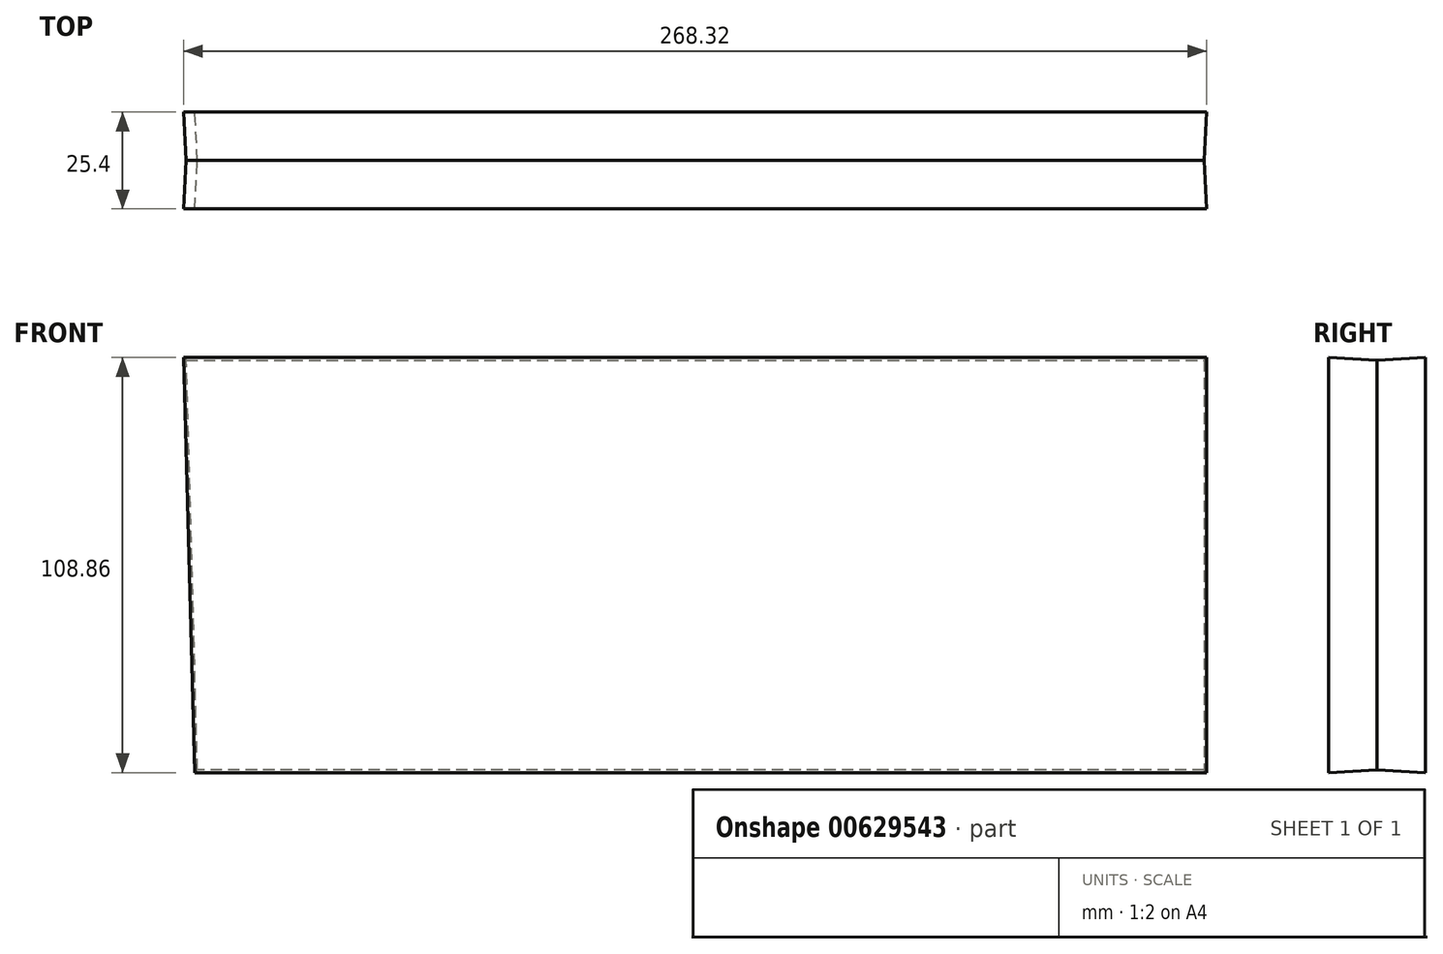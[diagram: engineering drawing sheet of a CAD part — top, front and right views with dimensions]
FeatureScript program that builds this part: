
annotation { "Feature Type Name" : "Feature", "Feature Type Description" : "" }
export const myFeature = defineFeature(function(context is Context, id is Id, definition is map)
    precondition{}
    {
        {
            var Q0;
            Q0=qCreatedBy(makeId("Front.planeOp"),FACE);
            var sketch = newSketch(context, id + "F0", { "sketchPlane" : qUnion([Q0])});
            skLineSegment(sketch, "E0", {"start": v(-119.06, 156.54) * mm, "end": v(147.91, 156.54) * mm});
            skLineSegment(sketch, "E1", {"start": v(147.91, 156.54) * mm, "end": v(147.91, 49.02) * mm});
            skLineSegment(sketch, "E2", {"start": v(147.91, 49.02) * mm, "end": v(-116.15, 49.02) * mm});
            skLineSegment(sketch, "E3", {"start": v(-116.15, 49.02) * mm, "end": v(-119.06, 156.54) * mm});
            skSolve(sketch);
        }
        {
            var Q0;
            Q0=makeQuery(id+"F0.imprint","IMPRINT",FACE,{"disambiguationData":[TD([[makeQuery(id+"F0.imprint","IMPRINT",EDGE,{"derivedFrom":sQuery(id+"F0.wireOp",EDGE,"E0")}),-1.0]])]});
            extrude(context, id + "F1", {"entities" : qUnion([Q0]), "endBound" : BoundingType.SYMMETRIC, "depth" : 25.4 * mm, "offsetDistance" : 25.4 * mm, "hasDraft" : true, "draftAngle" : 3 * degree});
        }
    });
